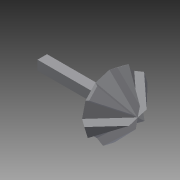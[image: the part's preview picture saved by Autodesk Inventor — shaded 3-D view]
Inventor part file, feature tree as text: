
AUTODESK INVENTOR PART (.ipt)
format: ipt  version: 2015 (Build 190159000, 159)  size: 155,648 bytes
history: native  units: in
note: dims shown in document units (in); Inventor stores cm internally (conversion verified against a paired STEP export)
features: extrude x4, sketch x4, pattern_circular x1
ambient origin geometry x8: Origin, YZ Plane, XZ Plane, XY Plane, X Axis, Y Axis, Z Axis, Center Point
bodies: Body1 (feature_tree)
feature tree (9):
  extrude  "Extrusion2"  Depth=0.24in
  extrude  "Extrusion3"  Depth=0.05in
  extrude  "Extrusion4"  Depth=0.07in
  extrude  "Extrusion5"  Depth=0.001in TaperAngle=0.0deg
  pattern_circular  "Circular Pattern1"  Count=6 Angle=360.0deg
  sketch  "Sketch6"  dims[d27=0.2in d28=0.24in d29=-0.3092in]
  sketch  "Sketch7"  dims[d30=0.29in d31=0.05in d32=-0.0687in]
  sketch  "Sketch8"  dims[d33=0.07in d34=0.07in]
  sketch  "Sketch9"  dims[d35=0.5in d36=0.0in d37=0.001in d38=0.0in d39=2.3622in d40=360.0deg]
